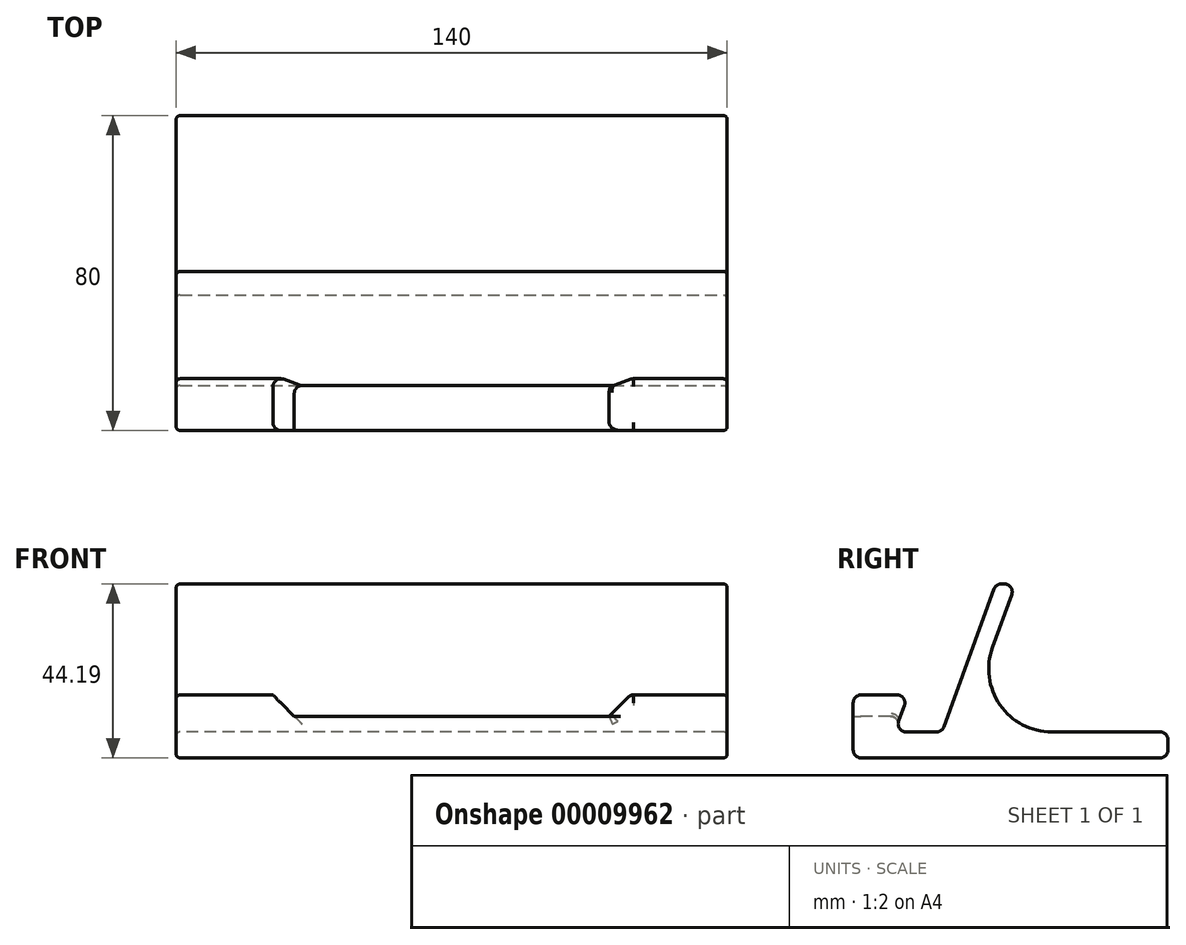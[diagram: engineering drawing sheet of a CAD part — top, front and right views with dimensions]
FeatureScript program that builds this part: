
annotation { "Feature Type Name" : "Feature", "Feature Type Description" : "" }
export const myFeature = defineFeature(function(context is Context, id is Id, definition is map)
    precondition{}
    {
        {
            var Q0;
            Q0=qCreatedBy(makeId("Right.planeOp"),FACE);
            var sketch = newSketch(context, id + "F0", { "sketchPlane" : qUnion([Q0])});
            skLineSegment(sketch, "E0.rect.top", {"start": v(40, 0) * mm, "end": v(-40, 0) * mm});
            skPoint(sketch, "E0.rect.middle", {"position": v(0, 0) * mm});
            skPoint(sketch, "E0.rect.right.start.orphan", {"position": v(-40, 0) * mm});
            skPoint(sketch, "E0.rect.left.start.orphan", {"position": v(40, 0) * mm});
            skLineSegment(sketch, "E1", {"start": v(-40, 0) * mm, "end": v(-40, 16) * mm});
            skLineSegment(sketch, "E2", {"start": v(-40, 16) * mm, "end": v(-40, 16) * mm});
            skLineSegment(sketch, "E3", {"start": v(-40, 16) * mm, "end": v(-26, 16) * mm});
            skLineSegment(sketch, "E4", {"start": v(-26, 16) * mm, "end": v(-26, 16) * mm});
            skLineSegment(sketch, "E5", {"start": v(-26, 16) * mm, "end": v(-29.42, 6.6) * mm});
            skLineSegment(sketch, "E6", {"start": v(-29.42, 6.6) * mm, "end": v(-17.42, 6.6) * mm});
            skLineSegment(sketch, "E7", {"start": v(-17.42, 6.6) * mm, "end": v(-3.74, 44.2) * mm});
            skLineSegment(sketch, "E8", {"start": v(-3.74, 44.2) * mm, "end": v(1.26, 44.2) * mm});
            skLineSegment(sketch, "E9", {"start": v(1.26, 44.2) * mm, "end": v(-12.42, 6.6) * mm});
            skLineSegment(sketch, "E10", {"start": v(-12.42, 6.6) * mm, "end": v(40, 6.6) * mm});
            skLineSegment(sketch, "E11", {"start": v(40, 6.6) * mm, "end": v(40, 0) * mm});
            skSolve(sketch);
        }
        {
            var Q0;
            Q0 = qSketchRegion(id + "F0", true);
            extrude(context, id + "F5", {"entities" : qUnion([Q0]), "depth" : 140 * mm});
        }
        {
            var Q0;
            Q0=makeQuery(id+"F5.opExtrude","SWEPT_EDGE",EDGE,{"disambiguationData":[OSD([sQuery(id+"F0.wireOp",EDGE,"E9"),sQuery(id+"F0.wireOp",EDGE,"E10")])]});
            fillet(context, id + "F6", {"entities" : qUnion([Q0]), "radius" : 16 * mm, "tangentPropagation" : true, "allowEdgeOverflow" : false});
        }
        {
            var Q0;
            Q0=makeQuery(id+"F5.opExtrude","SWEPT_EDGE",EDGE,{"disambiguationData":[OSD([sQuery(id+"F0.wireOp",EDGE,"E3"),sQuery(id+"F0.wireOp",EDGE,"E5")])]});
            var Q1;
            Q1=makeQuery(id+"F5.opExtrude","SWEPT_EDGE",EDGE,{"disambiguationData":[OSD([sQuery(id+"F0.wireOp",EDGE,"E5"),sQuery(id+"F0.wireOp",EDGE,"E6")])]});
            var Q2;
            Q2=makeQuery(id+"F5.opExtrude","SWEPT_EDGE",EDGE,{"disambiguationData":[OSD([sQuery(id+"F0.wireOp",EDGE,"E6"),sQuery(id+"F0.wireOp",EDGE,"E7")])]});
            var Q3;
            Q3=makeQuery(id+"F5.opExtrude","SWEPT_EDGE",EDGE,{"disambiguationData":[OSD([sQuery(id+"F0.wireOp",EDGE,"E10"),sQuery(id+"F0.wireOp",EDGE,"E11")])]});
            var Q4;
            Q4=makeQuery(id+"F5.opExtrude","SWEPT_EDGE",EDGE,{"disambiguationData":[OSD([sQuery(id+"F0.wireOp",EDGE,"E0.rect.top"),sQuery(id+"F0.wireOp",EDGE,"E11")])]});
            var Q5;
            Q5=makeQuery(id+"F5.opExtrude","SWEPT_EDGE",EDGE,{"disambiguationData":[OSD([sQuery(id+"F0.wireOp",EDGE,"E0.rect.top"),sQuery(id+"F0.wireOp",EDGE,"E1")])]});
            var Q6;
            Q6=makeQuery(id+"F5.opExtrude","SWEPT_EDGE",EDGE,{"disambiguationData":[OSD([sQuery(id+"F0.wireOp",EDGE,"E1"),sQuery(id+"F0.wireOp",EDGE,"E3")])]});
            var Q7;
            Q7=makeQuery(id+"F5.opExtrude","SWEPT_EDGE",EDGE,{"disambiguationData":[OSD([sQuery(id+"F0.wireOp",EDGE,"E7"),sQuery(id+"F0.wireOp",EDGE,"E8")])]});
            var Q8;
            Q8=makeQuery(id+"F5.opExtrude","SWEPT_EDGE",EDGE,{"disambiguationData":[OSD([sQuery(id+"F0.wireOp",EDGE,"E8"),sQuery(id+"F0.wireOp",EDGE,"E9")])]});
            fillet(context, id + "F1", {"entities" : qUnion([Q0, Q1, Q2, Q3, Q4, Q5, Q6, Q7, Q8]), "radius" : 2 * mm, "tangentPropagation" : true, "allowEdgeOverflow" : false});
        }
        {
            var Q0;
            Q0=makeQuery(id+"F5.opExtrude","SWEPT_FACE",FACE,{"disambiguationData":[OSD([sQuery(id+"F0.wireOp",EDGE,"E1")])]});
            var sketch = newSketch(context, id + "F7", { "sketchPlane" : qUnion([Q0])});
            skLineSegment(sketch, "E12.bottom", {"start": v(30, 10.6) * mm, "end": v(110, 10.6) * mm});
            skLineSegment(sketch, "E13", {"start": v(30, 10.6) * mm, "end": v(24.6, 16) * mm});
            skLineSegment(sketch, "E14", {"start": v(110, 10.6) * mm, "end": v(115.4, 16) * mm});
            skLineSegment(sketch, "E15", {"start": v(24.6, 16) * mm, "end": v(115.4, 16) * mm});
            skSolve(sketch);
        }
        {
            var Q0;
            Q0 = qSketchRegion(id + "F7", true);
            extrude(context, id + "F2", {"entities" : qUnion([Q0]), "operationType" : NewBodyOperationType.REMOVE, "oppositeDirection" : true, "depth" : 14 * mm});
        }
        {
            var Q0;
            Q0=makeQuery(id+"F2.boolean.opBoolean","COPY",EDGE,{"derivedFrom":makeQuery(id+"F2.opExtrude","CAP_EDGE",EDGE,{"disambiguationData":[OSD([sQuery(id+"F7.wireOp",EDGE,"E12.bottom")])],"isStart":true})});
            var Q1;
            Q1=makeQuery(id+"F2.boolean.opBoolean","INTERSECT",EDGE,{"derivedFrom":[makeQuery(id+"F5.opExtrude","SWEPT_FACE",FACE,{"disambiguationData":[OSD([sQuery(id+"F0.wireOp",EDGE,"E5")])]}),makeQuery(id+"F2.opExtrude","SWEPT_FACE",FACE,{"disambiguationData":[OSD([sQuery(id+"F7.wireOp",EDGE,"E12.bottom")])]})]});
            fillet(context, id + "F3", {"entities" : qUnion([Q0, Q1]), "radius" : 2 * mm, "tangentPropagation" : true, "allowEdgeOverflow" : false});
        }
        {
            var Q0;
            Q0=makeQuery(id+"F5.opExtrude","CAP_EDGE",EDGE,{"disambiguationData":[OSD([sQuery(id+"F0.wireOp",EDGE,"E1")])],"isStart":false});
            var Q1;
            Q1=makeQuery(id+"F5.opExtrude","CAP_EDGE",EDGE,{"disambiguationData":[OSD([sQuery(id+"F0.wireOp",EDGE,"E1")])],"isStart":true});
            fillet(context, id + "F4", {"entities" : qUnion([Q0, Q1]), "radius" : 1 * mm, "tangentPropagation" : true, "allowEdgeOverflow" : false});
        }
        {
            var Q0;
            Q0=makeQuery(id+"F2.boolean.opBoolean","COPY",EDGE,{"derivedFrom":makeQuery(id+"F2.opExtrude","SWEPT_EDGE",EDGE,{"disambiguationData":[OSD([sQuery(id+"F7.wireOp",EDGE,"E13"),sQuery(id+"F7.wireOp",EDGE,"E15")])]})});
            var Q1;
            Q1=makeQuery(id+"F2.boolean.opBoolean","COPY",EDGE,{"derivedFrom":makeQuery(id+"F2.opExtrude","SWEPT_EDGE",EDGE,{"disambiguationData":[OSD([sQuery(id+"F7.wireOp",EDGE,"E14"),sQuery(id+"F7.wireOp",EDGE,"E15")])]})});
            fillet(context, id + "F8", {"entities" : qUnion([Q0, Q1]), "radius" : 2 * mm, "tangentPropagation" : true, "allowEdgeOverflow" : false});
        }
    });
